# Revit family: BS101LEDECO-E
name_source: partatom
category: Lighting Fixtures
revit_build: Autodesk Revit LT 2017 (Build: 20160225_1515(x64)
units: mm (PartAtom-declared; Revit-internal decimal feet)

## family parameters
Cut with Voids When Loaded = No
Host = Face
Light Source = Yes
Part Type = Normal
Room Calculation Point = No
Round Connector Dimension = Use Diameter
Shared = No

## types (1)
- BS101LEDECO4HTHOWT40120V-277V
    Color Filter = 16777215
    Default Elevation = 4' - 0"
    Description = The ILLUMINA® BS101LED provides ideal illumination for canopies, warehouses, schools, breezeways and service corridors.

It is corrosion, flame and vandal resistant and features eight (8) closure clips that securely and evenly seal the luminaire.
    Dimming Lamp Color Temperature Shift = <None>
    Emit from Line Length = 2' - 0"
    Lamp = LED
    Manufacturer = BEGHELLI
    Model = BS101LEDECO-E
    Photometric Web File = BS101LEDECO-E4HTHOWT40120-277V.ies
    Tilt Angle = -90.00°
    Type Comments = ILLUMINA FAMILY
    Type Image = BS101LED PICTURE.JPG
    Wattage Comments = 35W

## geometry (parser evidence)
native form markers: Sweep x30
no freeform markers — native parametric forms only
